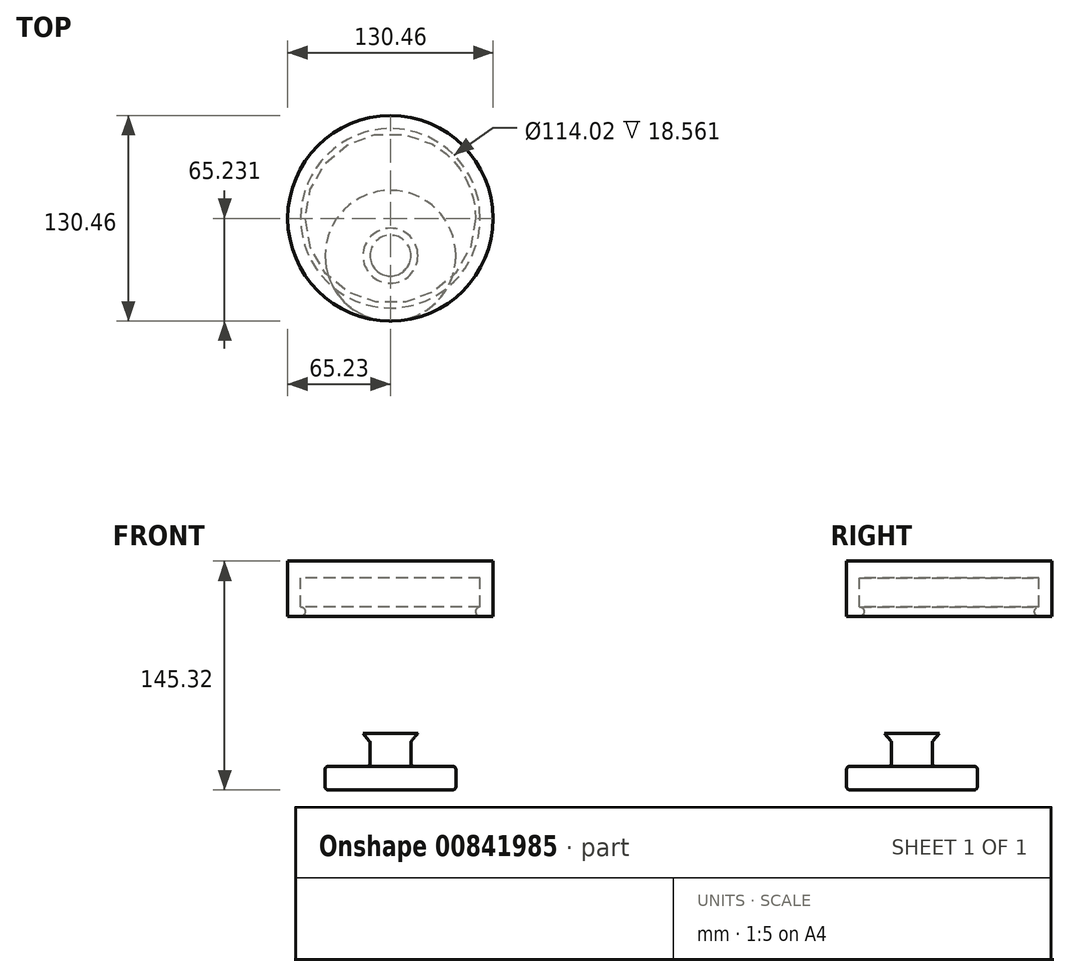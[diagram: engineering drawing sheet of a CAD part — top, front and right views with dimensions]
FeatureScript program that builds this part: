
annotation { "Feature Type Name" : "Feature", "Feature Type Description" : "" }
export const myFeature = defineFeature(function(context is Context, id is Id, definition is map)
    precondition{}
    {
        {
            var Q0;
            Q0=qCreatedBy(makeId("Right.planeOp"),FACE);
            var sketch = newSketch(context, id + "F0", { "sketchPlane" : qUnion([Q0])});
            skLineSegment(sketch, "E0", {"start": v(0, 0) * mm, "end": v(0, -15) * mm});
            skLineSegment(sketch, "E1", {"start": v(0, -15) * mm, "end": v(41.5, -15) * mm});
            skLineSegment(sketch, "E2", {"start": v(41.5, -15) * mm, "end": v(41.5, 0) * mm});
            skLineSegment(sketch, "E3", {"start": v(41.5, 0) * mm, "end": v(13, 0) * mm});
            skLineSegment(sketch, "E4", {"start": v(13, 0) * mm, "end": v(13, 15.7) * mm});
            skLineSegment(sketch, "E5", {"start": v(13, 15.7) * mm, "end": v(17.44, 21) * mm});
            skLineSegment(sketch, "E6", {"start": v(17.44, 21) * mm, "end": v(0, 21) * mm});
            skLineSegment(sketch, "E7", {"start": v(0, -4.63) * mm, "end": v(0, -40.63) * mm, "construction": true});
            skLineSegment(sketch, "E8", {"start": v(0, 21) * mm, "end": v(0, -15) * mm});
            skSolve(sketch);
        }
        {
            var Q0;
            {var subQ0=sQuery(id+"F0.wireOp",EDGE,"E1");Q0=makeQuery(id+"F0.imprint","IMPRINT",FACE,{"disambiguationData":[TD([[makeQuery(id+"F0.imprint","IMPRINT",EDGE,{"derivedFrom":subQ0}),1.0]])]});}
            var Q1;
            Q1=sQuery(id+"F0.wireOp",EDGE,"E7");
            revolve(context, id + "F1", {"surfaceOperationType" : NewSurfaceOperationType.NEW, "entities" : qUnion([Q0]), "axis" : qUnion([Q1]), "revolveType" : RevolveType.FULL});
        }
        {
            var Q0;
            Q0=makeQuery(id+"F1.opRevolve","SWEPT_EDGE",EDGE,{"disambiguationData":[OSD([sQuery(id+"F0.wireOp",EDGE,"E2"),sQuery(id+"F0.wireOp",EDGE,"E3")])]});
            var Q1;
            Q1=makeQuery(id+"F1.opRevolve","SWEPT_EDGE",EDGE,{"disambiguationData":[OSD([sQuery(id+"F0.wireOp",EDGE,"E4"),sQuery(id+"F0.wireOp",EDGE,"E5")])]});
            var Q2;
            Q2=makeQuery(id+"F1.opRevolve","SWEPT_EDGE",EDGE,{"disambiguationData":[OSD([sQuery(id+"F0.wireOp",EDGE,"E3"),sQuery(id+"F0.wireOp",EDGE,"E4")])]});
            var Q3;
            Q3=makeQuery(id+"F1.opRevolve","SWEPT_EDGE",EDGE,{"disambiguationData":[OSD([sQuery(id+"F0.wireOp",EDGE,"E1"),sQuery(id+"F0.wireOp",EDGE,"E2")])]});
            fillet(context, id + "F2", {"entities" : qUnion([Q0, Q1, Q2, Q3]), "radius" : 2 * mm, "tangentPropagation" : true, "allowEdgeOverflow" : false});
        }
        {
            var Q0;
            Q0=qCreatedBy(makeId("Right.planeOp"),FACE);
            var sketch = newSketch(context, id + "F3", { "sketchPlane" : qUnion([Q0])});
            skLineSegment(sketch, "E9.bottom", {"start": v(88.96, 95.32) * mm, "end": v(81.53, 95.32) * mm});
            skLineSegment(sketch, "E9.top", {"start": v(88.96, 130.32) * mm, "end": v(-41.5, 130.32) * mm});
            skLineSegment(sketch, "E9.left", {"start": v(88.96, 95.32) * mm, "end": v(88.96, 130.32) * mm});
            skLineSegment(sketch, "E9.right", {"start": v(-41.5, 95.32) * mm, "end": v(-41.5, 130.32) * mm});
            skPoint(sketch, "E9.middle", {"position": v(23.73, 112.82) * mm});
            skLineSegment(sketch, "E10", {"start": v(-33.28, 119.72) * mm, "end": v(81.53, 119.72) * mm});
            skLineSegment(sketch, "E11", {"start": v(81.53, 119.72) * mm, "end": v(81.53, 101.16) * mm});
            skLineSegment(sketch, "E12.trimOffspring", {"start": v(-33.28, 95.32) * mm, "end": v(-41.5, 95.32) * mm});
            skArc(sketch, "E13", {"start": v(-33.28, 95.32) * mm, "mid": v(-30.36, 98.24) * mm, "end": v(-33.28, 101.16) * mm});
            skArc(sketch, "E14", {"start": v(81.53, 101.16) * mm, "mid": v(78.62, 98.24) * mm, "end": v(81.53, 95.32) * mm});
            skLineSegment(sketch, "E15.trimOffspring", {"start": v(-33.28, 101.16) * mm, "end": v(-33.28, 119.72) * mm});
            skLineSegment(sketch, "E16", {"start": v(23.73, 130.32) * mm, "end": v(23.73, 119.72) * mm});
            skSolve(sketch);
        }
        {
            var Q0;
            {var subQ3=sQuery(id+"F3.wireOp",EDGE,"E9.right");Q0=makeQuery(id+"F3.imprint","IMPRINT",FACE,{"disambiguationData":[TD([[makeQuery(id+"F3.imprint","IMPRINT",EDGE,{"derivedFrom":subQ3}),-1.0]])]});}
            var Q1;
            Q1=sQuery(id+"F3.wireOp",EDGE,"E16");
            revolve(context, id + "F4", {"surfaceOperationType" : NewSurfaceOperationType.NEW, "entities" : qUnion([Q0]), "axis" : qUnion([Q1]), "revolveType" : RevolveType.FULL});
        }
    });
